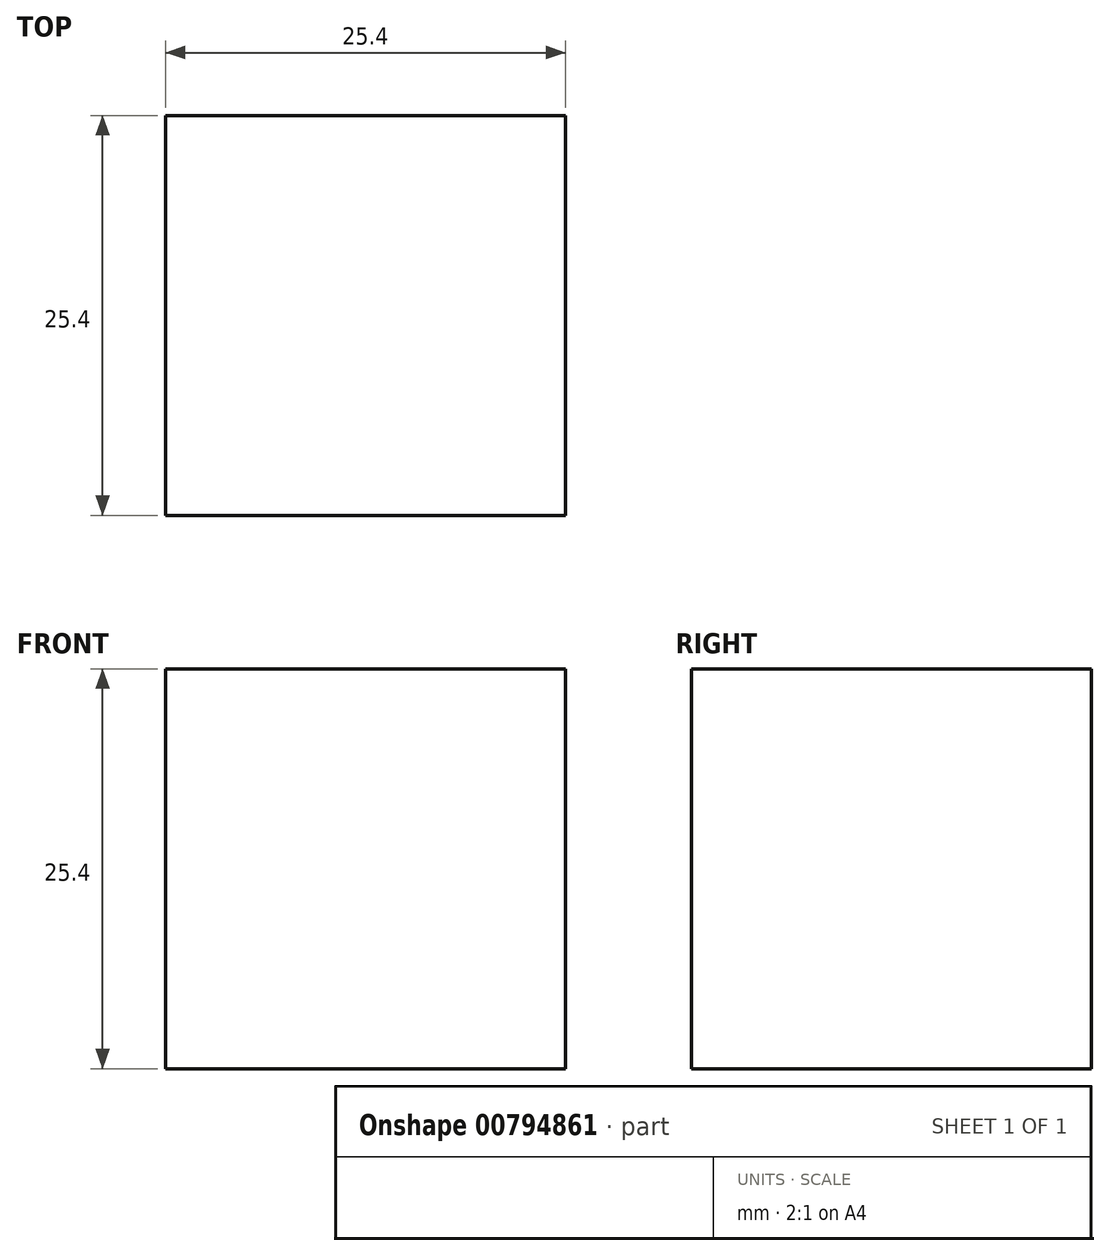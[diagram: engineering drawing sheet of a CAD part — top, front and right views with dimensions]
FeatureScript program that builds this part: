
annotation { "Feature Type Name" : "Feature", "Feature Type Description" : "" }
export const myFeature = defineFeature(function(context is Context, id is Id, definition is map)
    precondition{}
    {
        {
            var Q0;
            Q0=qCreatedBy(makeId("Top.planeOp"),FACE);
            var sketch = newSketch(context, id + "F0", { "sketchPlane" : qUnion([Q0])});
            skLineSegment(sketch, "E0.bottom", {"start": v(12.7, -12.7) * mm, "end": v(-12.7, -12.7) * mm});
            skLineSegment(sketch, "E0.top", {"start": v(12.7, 12.7) * mm, "end": v(-12.7, 12.7) * mm});
            skLineSegment(sketch, "E0.left", {"start": v(12.7, -12.7) * mm, "end": v(12.7, 12.7) * mm});
            skLineSegment(sketch, "E0.right", {"start": v(-12.7, -12.7) * mm, "end": v(-12.7, 12.7) * mm});
            skPoint(sketch, "E0.middle", {"position": v(0, 0) * mm});
            skSolve(sketch);
        }
        {
            var Q0;
            Q0 = qSketchRegion(id + "F0", true);
            extrude(context, id + "F1", {"entities" : qUnion([Q0]), "endBound" : BoundingType.SYMMETRIC, "depth" : 25.4 * mm, "offsetDistance" : 25.4 * mm});
        }
    });
